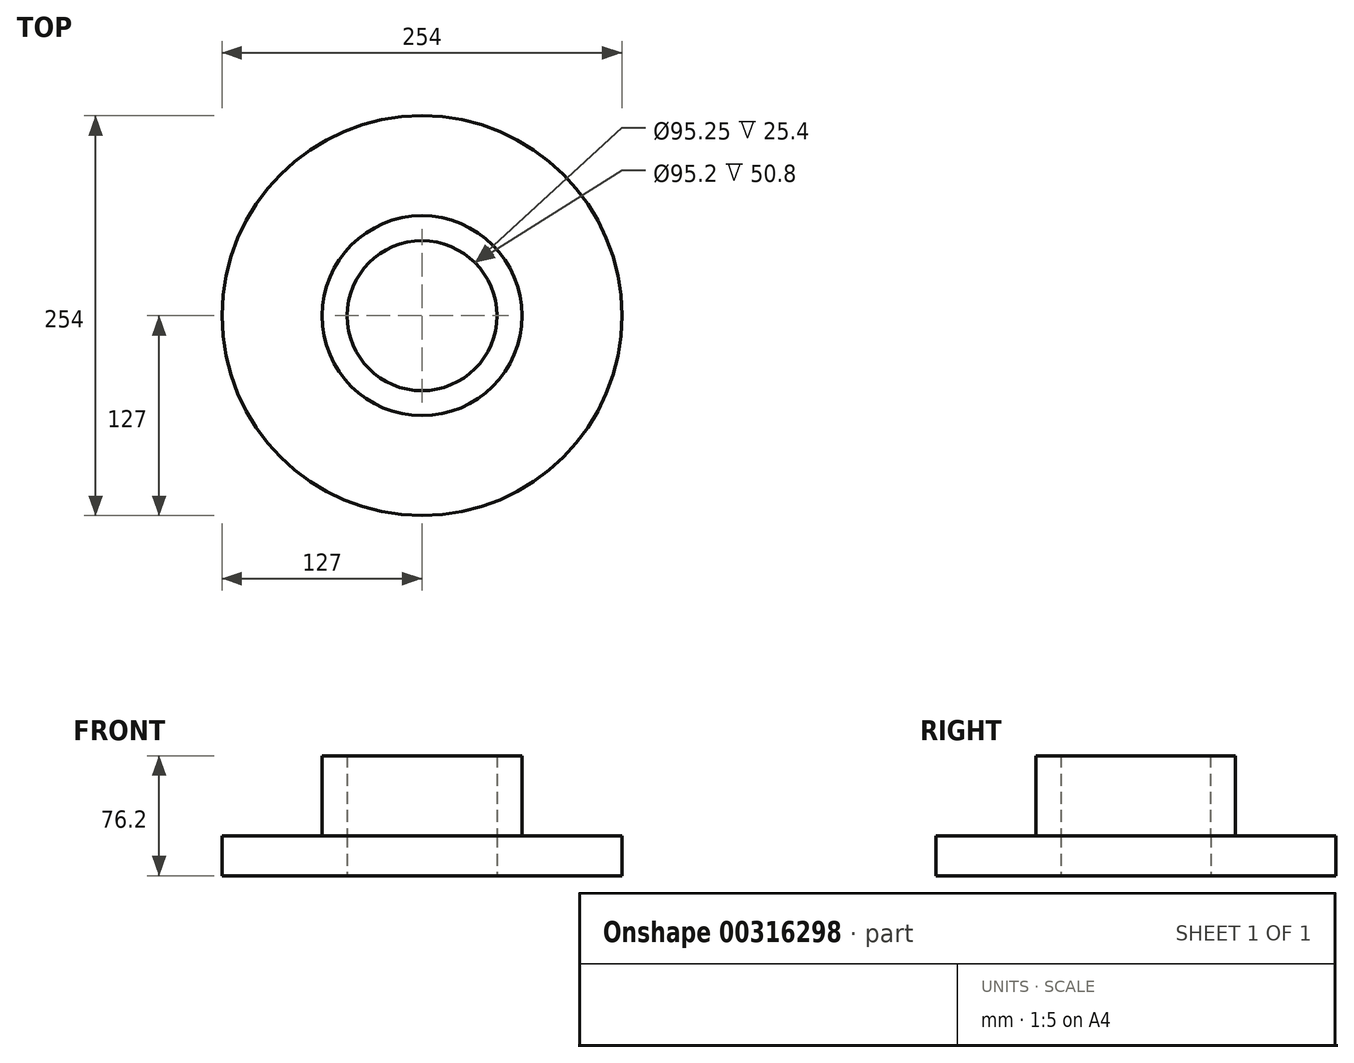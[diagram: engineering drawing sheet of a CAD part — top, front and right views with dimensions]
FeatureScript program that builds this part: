
annotation { "Feature Type Name" : "Feature", "Feature Type Description" : "" }
export const myFeature = defineFeature(function(context is Context, id is Id, definition is map)
    precondition{}
    {
        {
            var Q0;
            Q0=qCreatedBy(makeId("Top.planeOp"),FACE);
            var sketch = newSketch(context, id + "F0", { "sketchPlane" : qUnion([Q0])});
            skCircle(sketch, "E0", {"center": v(0, 0) * mm, "radius": 127 * mm});
            skCircle(sketch, "E1", {"center": v(0, 0) * mm, "radius": 47.63 * mm});
            skCircle(sketch, "E2", {"center": v(0, 0) * mm, "radius": 31.75 * mm});
            skSolve(sketch);
        }
        {
            var Q0;
            Q0=makeQuery(id+"F0.imprint","IMPRINT",FACE,{"disambiguationData":[TD([[makeQuery(id+"F0.imprint","IMPRINT",EDGE,{"derivedFrom":sQuery(id+"F0.wireOp",EDGE,"E0")}),1.0]])]});
            extrude(context, id + "F1", {"entities" : qUnion([Q0]), "depth" : 25.4 * mm});
        }
        {
            var Q0;
            Q0=makeQuery(id+"F1.opExtrude","CAP_FACE",FACE,{"disambiguationData":[OSD([sQuery(id+"F0.wireOp",EDGE,"E0"),sQuery(id+"F0.wireOp",EDGE,"E1")])],"isStart":false});
            var sketch = newSketch(context, id + "F2", { "sketchPlane" : qUnion([Q0])});
            skCircle(sketch, "E3", {"center": v(0, 0) * mm, "radius": 63.5 * mm});
            skCircle(sketch, "E4", {"center": v(0, 0) * mm, "radius": 47.63 * mm});
            skSolve(sketch);
        }
        {
            var Q0;
            Q0=makeQuery(id+"F2.imprint","IMPRINT",FACE,{"disambiguationData":[TD([[makeQuery(id+"F2.imprint","IMPRINT",EDGE,{"derivedFrom":sQuery(id+"F2.wireOp",EDGE,"E3")}),-1.0]])]});
            var sketch = newSketch(context, id + "F3", { "sketchPlane" : qUnion([Q0])});
            skCircle(sketch, "E5", {"center": v(0, 0) * mm, "radius": 63.48 * mm});
            skCircle(sketch, "E6", {"center": v(0, 0) * mm, "radius": 47.6 * mm});
            skSolve(sketch);
        }
        {
            var Q0;
            Q0 = qSketchRegion(id + "F3", true);
            extrude(context, id + "F4", {"entities" : qUnion([Q0]), "operationType" : NewBodyOperationType.ADD, "depth" : 50.8 * mm});
        }
        {
            var Q0;
            Q0=makeQuery(id+"F2.imprint","IMPRINT",FACE,{"disambiguationData":[TD([[makeQuery(id+"F2.imprint","IMPRINT",EDGE,{"derivedFrom":sQuery(id+"F2.wireOp",EDGE,"E3")}),-1.0]])]});
            var sketch = newSketch(context, id + "F5", { "sketchPlane" : qUnion([Q0])});
            skCircle(sketch, "E7", {"center": v(0, 92.3) * mm, "radius": 14.65 * mm});
            skCircle(sketch, "E8", {"center": v(0, 92.3) * mm, "radius": 9.76 * mm});
            skSolve(sketch);
        }
        {
            var Q0;
            Q0=sQuery(id+"F5.wireOp",EDGE,"E7");
            var Q1;
            Q1=sQuery(id+"F5.wireOp",EDGE,"E8");
            extrude(context, id + "F6", {"bodyType" : ToolBodyType.SURFACE, "surfaceEntities" : qUnion([Q0, Q1]), "depth" : 25.4 * mm});
        }
    });
